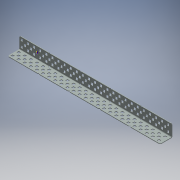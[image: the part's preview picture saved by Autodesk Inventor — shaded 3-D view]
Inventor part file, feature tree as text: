
AUTODESK INVENTOR PART (.ipt)
format: ipt  version: 2018 (Build 220112000, 112)  size: 1,527,808 bytes
history: native  units: mm (DEFAULTED — no unit token found)
features: other x154, extrude x148, sketch x12, pattern_linear x4, sheet_metal_op x3
ambient origin geometry x8: Origin, YZ Plane, XZ Plane, XY Plane, X Axis, Y Axis, Z Axis, Center Point
bodies: Solid1 (feature_tree)
feature tree (321):
  sheet_metal_op  "Face2"
  sheet_metal_op  "Flange8"
  pattern_linear  "Rectangular Pattern1"  Count1=24 Spacing1=12.7mm
  pattern_linear  "Rectangular Pattern2"  Spacing1=9.144mm  [1 undecoded]
  pattern_linear  "Rectangular Pattern3"  Spacing1=15.494mm  [1 undecoded]
  pattern_linear  "Rectangular Pattern4"  Spacing1=4.572mm  [1 undecoded]
  sketch  "Sketch23"  dims[d128=4.572mm]
  sketch  "Sketch24"  dims[d129=9.017mm d130=9.144mm d133=15.494mm d134=4.572mm d136=1.27mm d138=1.27mm d139=0.635mm d140=2.54mm d141=1.27mm d142=25.4mm d143=90.0deg d144=1.27mm d145=5.08mm d146=1.27mm d147=1.27mm d148=2.921mm d149=4.572mm d150=8.128mm d151=4.572mm d152=2.794mm d153=4.572mm d154=9.144mm d155=4.572mm d156=4.572mm d157=15.494mm d158=4.572mm d159=9.017mm d160=240.0mm d162=12.7mm d163=10.0mm d165=25.4mm d167=1.27mm d168=0.0mm d169=1.905mm d170=60.0mm d172=63.5mm d173=10.0mm d175=25.4mm d177=1.27mm d178=0.0mm d179=1.905mm d180=60.0mm d182=63.5mm d183=10.0mm d185=25.4mm d187=1.27mm d188=0.0mm d189=1.1176mm d190=1.905mm d191=40.0mm d193=63.5mm d194=10.0mm d196=25.4mm d198=1.27mm d199=0.0mm d200=25.4mm d201=0.0mm d202=250.0mm d204=12.7mm d205=20.0mm d207=12.7mm d208=25.4mm d209=0.0mm d210=240.0mm d212=12.7mm d213=0.0mm d214=0.0mm d215=0.0mm d216=0.0mm d217=0.0mm d218=0.0mm d219=0.0mm d220=0.0mm d221=0.0mm d222=0.0mm d223=0.0mm d224=0.0mm d225=0.0mm d226=0.0mm d227=0.0mm d228=0.0mm d229=0.0mm d230=0.0mm d231=0.0mm d232=0.0mm d233=0.0mm d234=0.0mm d235=0.0mm d236=0.0mm d237=0.0mm d238=0.0mm d239=0.0mm d240=0.0mm d241=0.0mm d242=0.0mm d243=0.0mm d244=0.0mm d245=0.0mm d246=0.0mm d247=0.0mm d248=0.0mm d249=0.0mm d250=0.0mm d251=0.0mm d252=0.0mm d253=0.0mm d254=0.0mm d255=0.0mm d256=0.0mm d257=0.0mm d258=0.0mm d259=0.0mm d260=0.0mm d261=0.0mm d262=0.0mm d263=0.0mm d264=0.0mm d265=0.0mm d266=0.0mm d267=0.0mm d268=0.0mm d269=0.0mm d270=0.0mm d271=0.0mm d272=0.0mm d273=0.0mm d274=0.0mm d275=0.0mm d276=0.0mm d277=0.0mm d278=0.0mm d279=0.0mm d280=0.0mm d281=0.0mm d282=0.0mm d283=0.0mm d284=0.0mm d285=0.0mm d286=0.0mm d287=0.0mm d288=0.0mm d289=0.0mm d290=0.0mm d291=0.0mm d292=0.0mm d293=0.0mm d294=0.0mm d295=0.0mm d296=0.0mm d297=0.0mm d298=0.0mm d299=0.0mm d300=0.0mm d301=0.0mm d302=0.0mm d303=0.0mm d304=0.0mm d305=0.0mm d306=0.0mm d307=0.0mm d308=0.0mm d309=0.0mm d310=0.0mm d311=0.0mm d312=0.0mm d313=0.0mm d314=0.0mm d315=0.0mm d316=0.0mm d317=0.0mm d318=0.0mm d319=0.0mm d320=0.0mm d321=0.0mm d322=0.0mm d323=0.0mm d324=0.0mm d325=0.0mm d326=0.0mm d327=0.0mm d328=0.0mm d329=0.0mm d330=0.0mm d331=0.0mm d332=0.0mm d333=0.0mm d334=0.0mm d335=0.0mm d336=0.0mm d337=0.0mm d338=0.0mm d339=0.0mm d340=0.0mm d341=0.0mm d342=0.0mm d343=0.0mm d344=0.0mm d345=0.0mm d346=0.0mm d347=0.0mm d348=0.0mm d349=0.0mm d350=0.0mm d351=0.0mm d352=0.0mm d353=0.0mm d354=0.0mm d355=0.0mm d356=0.0mm d357=0.0mm d358=0.0mm d359=0.0mm d360=25.4mm d361=0.0mm d362=250.0mm d364=12.7mm d365=20.0mm d367=12.7mm d368=25.4mm d369=0.0mm d370=240.0mm d372=12.7mm d373=0.0mm d374=0.0mm d375=0.0mm d376=0.0mm d377=0.0mm d378=0.0mm d379=0.0mm d380=0.0mm d381=0.0mm d382=0.0mm d383=0.0mm d384=0.0mm d385=0.0mm d386=0.0mm d387=0.0mm d388=0.0mm d389=0.0mm d390=0.0mm d391=0.0mm d392=0.0mm d393=0.0mm d394=0.0mm d395=0.0mm d396=0.0mm d397=0.0mm d398=0.0mm d399=0.0mm d400=0.0mm d401=0.0mm d402=0.0mm d403=0.0mm d404=0.0mm d405=0.0mm d406=0.0mm d407=0.0mm d408=0.0mm d409=0.0mm d410=0.0mm d411=0.0mm d412=0.0mm d413=0.0mm d414=0.0mm d415=0.0mm d416=0.0mm d417=0.0mm d418=0.0mm d419=0.0mm d420=0.0mm d421=0.0mm d422=0.0mm d423=0.0mm d424=0.0mm d425=0.0mm d426=0.0mm d427=0.0mm d428=0.0mm d429=0.0mm d430=0.0mm d431=0.0mm d432=0.0mm d433=0.0mm d434=0.0mm d435=0.0mm d436=0.0mm d437=0.0mm d438=0.0mm d439=0.0mm d440=0.0mm d441=0.0mm d442=0.0mm d443=0.0mm d444=0.0mm d445=0.0mm d446=0.0mm d447=0.0mm d448=0.0mm d449=0.0mm d450=0.0mm d451=0.0mm d452=0.0mm d453=0.0mm d454=0.0mm d455=0.0mm d456=0.0mm d457=0.0mm d458=0.0mm d459=0.0mm d460=0.0mm d461=0.0mm d462=0.0mm d463=0.0mm d464=0.0mm d465=0.0mm d466=0.0mm d467=0.0mm d468=0.0mm d469=0.0mm d470=0.0mm d471=0.0mm d472=0.0mm d473=0.0mm d474=0.0mm d475=0.0mm d476=0.0mm d477=0.0mm d478=0.0mm d479=0.0mm d480=0.0mm d481=0.0mm d482=0.0mm d483=0.0mm d484=0.0mm d485=0.0mm d486=0.0mm d487=0.0mm d488=0.0mm d489=0.0mm d490=0.0mm d491=0.0mm d492=0.0mm d493=0.0mm d494=0.0mm d495=0.0mm d496=0.0mm d497=0.0mm d498=0.0mm d499=0.0mm d500=0.0mm d501=0.0mm d502=0.0mm d503=0.0mm d504=0.0mm d505=0.0mm d506=0.0mm d507=0.0mm d508=0.0mm d509=0.0mm d510=0.0mm d511=0.0mm d512=0.0mm d513=0.0mm d514=0.0mm d515=0.0mm d516=0.0mm d517=0.0mm d518=0.0mm d519=0.0mm d520=0.0mm d521=1.27mm]
  sketch  "Sketch1"  dims[d20=2.794mm]
  other  "Plate9"
  sketch  "Sketch14"  dims[d22=2.921mm]
  other  "Plate10"
  sheet_metal_op  "Bend8"
  sketch  "Sketch15"  dims[d23=22.86mm]
  sketch  "Sketch16"  dims[d24=4.572mm]
  sketch  "Sketch17"  dims[d25=8.128mm]
  sketch  "Sketch18"  dims[d26=4.572mm]
  sketch  "Sketch19"  dims[d27=1.27mm]
  other  "Srf1"
  other  "Srf2"
  other  "Srf3"
  other  "Srf4"
  other  "Srf5"
  other  "Srf6"
  other  "Srf7"
  other  "Srf8"
  other  "Srf9"
  other  "Srf10"
  other  "Srf11"
  other  "Srf12"
  other  "Srf13"
  other  "Srf14"
  other  "Srf15"
  other  "Srf16"
  other  "Srf17"
  other  "Srf18"
  other  "Srf19"
  other  "Srf20"
  other  "Srf21"
  other  "Srf22"
  other  "Srf23"
  other  "Srf24"
  other  "Srf25"
  other  "Srf26"
  other  "Srf27"
  other  "Srf28"
  other  "Srf29"
  other  "Srf30"
  other  "Srf31"
  other  "Srf32"
  other  "Srf33"
  other  "Srf34"
  other  "Srf35"
  other  "Srf36"
  other  "Srf37"
  other  "Srf38"
  other  "Srf39"
  other  "Srf40"
  other  "Srf41"
  other  "Srf42"
  other  "Srf43"
  other  "Srf44"
  other  "Srf45"
  other  "Srf46"
  other  "Srf47"
  other  "Srf48"
  other  "Srf49"
  other  "Srf50"
  sketch  "Sketch20"  dims[d125=317.5mm]
  other  "Srf51"
  other  "Srf52"
  other  "Srf53"
  other  "Srf54"
  other  "Srf55"
  other  "Srf56"
  other  "Srf57"
  other  "Srf58"
  other  "Srf59"
  other  "Srf60"
  other  "Srf61"
  other  "Srf62"
  other  "Srf63"
  other  "Srf64"
  other  "Srf65"
  other  "Srf66"
  other  "Srf67"
  other  "Srf68"
  other  "Srf69"
  other  "Srf70"
  other  "Srf71"
  other  "Srf72"
  other  "Srf73"
  other  "Srf74"
  sketch  "Sketch21"  dims[d126=4.572mm]
  other  "Srf75"
  other  "Srf76"
  other  "Srf77"
  other  "Srf78"
  other  "Srf79"
  other  "Srf80"
  other  "Srf81"
  other  "Srf82"
  other  "Srf83"
  other  "Srf84"
  other  "Srf85"
  other  "Srf86"
  other  "Srf87"
  other  "Srf88"
  other  "Srf89"
  other  "Srf90"
  other  "Srf91"
  other  "Srf92"
  other  "Srf93"
  other  "Srf94"
  other  "Srf95"
  other  "Srf96"
  other  "Srf97"
  other  "Srf98"
  other  "Srf99"
  other  "Srf100"
  other  "Srf101"
  other  "Srf102"
  other  "Srf103"
  other  "Srf104"
  other  "Srf105"
  other  "Srf106"
  other  "Srf107"
  other  "Srf108"
  other  "Srf109"
  other  "Srf110"
  other  "Srf111"
  other  "Srf112"
  other  "Srf113"
  other  "Srf114"
  other  "Srf115"
  other  "Srf116"
  other  "Srf117"
  other  "Srf118"
  other  "Srf119"
  other  "Srf120"
  other  "Srf121"
  other  "Srf122"
  other  "Srf123"
  other  "Srf124"
  sketch  "Sketch22"  dims[d127=4.572mm]
  other  "Srf125"
  other  "Srf126"
  other  "Srf127"
  other  "Srf128"
  other  "Srf129"
  other  "Srf130"
  other  "Srf131"
  other  "Srf132"
  other  "Srf133"
  other  "Srf134"
  other  "Srf135"
  other  "Srf136"
  other  "Srf137"
  other  "Srf138"
  other  "Srf139"
  other  "Srf140"
  other  "Srf141"
  other  "Srf142"
  other  "Srf143"
  other  "Srf144"
  other  "Srf145"
  other  "Srf146"
  other  "Srf147"
  other  "Srf148"
  other  "Cut4"
  other  "Cut5"
  other  "Cut6"
  other  "Cut7"
  extrude  "ExtrusionSrf1"  Depth=10.0mm
  extrude  "ExtrusionSrf51"  Depth=10.0mm
  extrude  "ExtrusionSrf75"  Depth=10.0mm
  extrude  "ExtrusionSrf125"  Depth=10.0mm
  extrude  "ExtrusionSrf2"  Depth=10.0mm
  extrude  "ExtrusionSrf3"  Depth=10.0mm TaperAngle=90.0deg
  extrude  "ExtrusionSrf4"  Depth=10.0mm
  extrude  "ExtrusionSrf5"  Depth=10.0mm
  extrude  "ExtrusionSrf6"  Depth=10.0mm
  extrude  "ExtrusionSrf7"  Depth=10.0mm
  extrude  "ExtrusionSrf8"  Depth=10.0mm
  extrude  "ExtrusionSrf9"  Depth=10.0mm
  extrude  "ExtrusionSrf10"  Depth=10.0mm
  extrude  "ExtrusionSrf11"  Depth=10.0mm
  extrude  "ExtrusionSrf12"  Depth=10.0mm
  extrude  "ExtrusionSrf13"  Depth=10.0mm
  extrude  "ExtrusionSrf14"  Depth=10.0mm
  extrude  "ExtrusionSrf15"  Depth=10.0mm
  extrude  "ExtrusionSrf16"  Depth=10.0mm
  extrude  "ExtrusionSrf17"  Depth=10.0mm
  extrude  "ExtrusionSrf18"  Depth=10.0mm
  extrude  "ExtrusionSrf19"  Depth=10.0mm
  extrude  "ExtrusionSrf20"  Depth=10.0mm
  extrude  "ExtrusionSrf21"  TaperAngle=0.0deg  [1 undecoded]
  extrude  "ExtrusionSrf22"  Depth=10.0mm
  extrude  "ExtrusionSrf23"  Depth=10.0mm
  extrude  "ExtrusionSrf24"  Depth=10.0mm
  extrude  "ExtrusionSrf25"  TaperAngle=0.0deg  [1 undecoded]
  extrude  "ExtrusionSrf26"  Depth=10.0mm
  extrude  "ExtrusionSrf27"  Depth=10.0mm
  extrude  "ExtrusionSrf28"  Depth=10.0mm
  extrude  "ExtrusionSrf29"  TaperAngle=0.0deg  [1 undecoded]
  extrude  "ExtrusionSrf30"  Depth=10.0mm
  extrude  "ExtrusionSrf31"  Depth=10.0mm
  extrude  "ExtrusionSrf32"  Depth=10.0mm
  extrude  "ExtrusionSrf33"  Depth=10.0mm
  extrude  "ExtrusionSrf34"  TaperAngle=0.0deg  [1 undecoded]
  extrude  "ExtrusionSrf35"  Depth=10.0mm TaperAngle=0.0deg
  extrude  "ExtrusionSrf36"  Depth=10.0mm
  extrude  "ExtrusionSrf37"  Depth=10.0mm
  extrude  "ExtrusionSrf38"  Depth=10.0mm TaperAngle=0.0deg
  extrude  "ExtrusionSrf39"  Depth=10.0mm
  extrude  "ExtrusionSrf40"  TaperAngle=0.0deg  [1 undecoded]
  extrude  "ExtrusionSrf41"  TaperAngle=0.0deg  [1 undecoded]
  extrude  "ExtrusionSrf42"  TaperAngle=0.0deg  [1 undecoded]
  extrude  "ExtrusionSrf43"  TaperAngle=0.0deg  [1 undecoded]
  extrude  "ExtrusionSrf44"  TaperAngle=0.0deg  [1 undecoded]
  extrude  "ExtrusionSrf45"  TaperAngle=0.0deg  [1 undecoded]
  extrude  "ExtrusionSrf46"  TaperAngle=0.0deg  [1 undecoded]
  extrude  "ExtrusionSrf47"  TaperAngle=0.0deg  [1 undecoded]
  extrude  "ExtrusionSrf48"  TaperAngle=0.0deg  [1 undecoded]
  extrude  "ExtrusionSrf49"  TaperAngle=0.0deg  [1 undecoded]
  extrude  "ExtrusionSrf50"  TaperAngle=0.0deg  [1 undecoded]
  extrude  "ExtrusionSrf52"  TaperAngle=0.0deg  [1 undecoded]
  extrude  "ExtrusionSrf53"  TaperAngle=0.0deg  [1 undecoded]
  extrude  "ExtrusionSrf54"  TaperAngle=0.0deg  [1 undecoded]
  extrude  "ExtrusionSrf55"  TaperAngle=0.0deg  [1 undecoded]
  extrude  "ExtrusionSrf56"  TaperAngle=0.0deg  [1 undecoded]
  extrude  "ExtrusionSrf57"  TaperAngle=0.0deg  [1 undecoded]
  extrude  "ExtrusionSrf58"  TaperAngle=0.0deg  [1 undecoded]
  extrude  "ExtrusionSrf59"  TaperAngle=0.0deg  [1 undecoded]
  extrude  "ExtrusionSrf60"  TaperAngle=0.0deg  [1 undecoded]
  extrude  "ExtrusionSrf61"  TaperAngle=0.0deg  [1 undecoded]
  extrude  "ExtrusionSrf62"  TaperAngle=0.0deg  [1 undecoded]
  extrude  "ExtrusionSrf63"  TaperAngle=0.0deg  [1 undecoded]
  extrude  "ExtrusionSrf64"  TaperAngle=0.0deg  [1 undecoded]
  extrude  "ExtrusionSrf65"  TaperAngle=0.0deg  [1 undecoded]
  extrude  "ExtrusionSrf66"  TaperAngle=0.0deg  [1 undecoded]
  extrude  "ExtrusionSrf67"  TaperAngle=0.0deg  [1 undecoded]
  extrude  "ExtrusionSrf68"  TaperAngle=0.0deg  [1 undecoded]
  extrude  "ExtrusionSrf69"  TaperAngle=0.0deg  [1 undecoded]
  extrude  "ExtrusionSrf70"  TaperAngle=0.0deg  [1 undecoded]
  extrude  "ExtrusionSrf71"  TaperAngle=0.0deg  [1 undecoded]
  extrude  "ExtrusionSrf72"  TaperAngle=0.0deg  [1 undecoded]
  extrude  "ExtrusionSrf73"  TaperAngle=0.0deg  [1 undecoded]
  extrude  "ExtrusionSrf74"  TaperAngle=0.0deg  [1 undecoded]
  extrude  "ExtrusionSrf76"  TaperAngle=0.0deg  [1 undecoded]
  extrude  "ExtrusionSrf77"  TaperAngle=0.0deg  [1 undecoded]
  extrude  "ExtrusionSrf78"  TaperAngle=0.0deg  [1 undecoded]
  extrude  "ExtrusionSrf79"  TaperAngle=0.0deg  [1 undecoded]
  extrude  "ExtrusionSrf80"  TaperAngle=0.0deg  [1 undecoded]
  extrude  "ExtrusionSrf81"  TaperAngle=0.0deg  [1 undecoded]
  extrude  "ExtrusionSrf82"  TaperAngle=0.0deg  [1 undecoded]
  extrude  "ExtrusionSrf83"  TaperAngle=0.0deg  [1 undecoded]
  extrude  "ExtrusionSrf84"  TaperAngle=0.0deg  [1 undecoded]
  extrude  "ExtrusionSrf85"  TaperAngle=0.0deg  [1 undecoded]
  extrude  "ExtrusionSrf86"  TaperAngle=0.0deg  [1 undecoded]
  extrude  "ExtrusionSrf87"  TaperAngle=0.0deg  [1 undecoded]
  extrude  "ExtrusionSrf88"  TaperAngle=0.0deg  [1 undecoded]
  extrude  "ExtrusionSrf89"  TaperAngle=0.0deg  [1 undecoded]
  extrude  "ExtrusionSrf90"  TaperAngle=0.0deg  [1 undecoded]
  extrude  "ExtrusionSrf91"  TaperAngle=0.0deg  [1 undecoded]
  extrude  "ExtrusionSrf92"  TaperAngle=0.0deg  [1 undecoded]
  extrude  "ExtrusionSrf93"  TaperAngle=0.0deg  [1 undecoded]
  extrude  "ExtrusionSrf94"  TaperAngle=0.0deg  [1 undecoded]
  extrude  "ExtrusionSrf95"  TaperAngle=0.0deg  [1 undecoded]
  extrude  "ExtrusionSrf96"  TaperAngle=0.0deg  [1 undecoded]
  extrude  "ExtrusionSrf97"  TaperAngle=0.0deg  [1 undecoded]
  extrude  "ExtrusionSrf98"  TaperAngle=0.0deg  [1 undecoded]
  extrude  "ExtrusionSrf99"  TaperAngle=0.0deg  [1 undecoded]
  extrude  "ExtrusionSrf100"  TaperAngle=0.0deg  [1 undecoded]
  extrude  "ExtrusionSrf101"  TaperAngle=0.0deg  [1 undecoded]
  extrude  "ExtrusionSrf102"  TaperAngle=0.0deg  [1 undecoded]
  extrude  "ExtrusionSrf103"  TaperAngle=0.0deg  [1 undecoded]
  extrude  "ExtrusionSrf104"  TaperAngle=0.0deg  [1 undecoded]
  extrude  "ExtrusionSrf105"  TaperAngle=0.0deg  [1 undecoded]
  extrude  "ExtrusionSrf106"  TaperAngle=0.0deg  [1 undecoded]
  extrude  "ExtrusionSrf107"  TaperAngle=0.0deg  [1 undecoded]
  extrude  "ExtrusionSrf108"  TaperAngle=0.0deg  [1 undecoded]
  extrude  "ExtrusionSrf109"  TaperAngle=0.0deg  [1 undecoded]
  extrude  "ExtrusionSrf110"  TaperAngle=0.0deg  [1 undecoded]
  extrude  "ExtrusionSrf111"  TaperAngle=0.0deg  [1 undecoded]
  extrude  "ExtrusionSrf112"  TaperAngle=0.0deg  [1 undecoded]
  extrude  "ExtrusionSrf113"  TaperAngle=0.0deg  [1 undecoded]
  extrude  "ExtrusionSrf114"  TaperAngle=0.0deg  [1 undecoded]
  extrude  "ExtrusionSrf115"  TaperAngle=0.0deg  [1 undecoded]
  extrude  "ExtrusionSrf116"  TaperAngle=0.0deg  [1 undecoded]
  extrude  "ExtrusionSrf117"  TaperAngle=0.0deg  [1 undecoded]
  extrude  "ExtrusionSrf118"  TaperAngle=0.0deg  [1 undecoded]
  extrude  "ExtrusionSrf119"  TaperAngle=0.0deg  [1 undecoded]
  extrude  "ExtrusionSrf120"  TaperAngle=0.0deg  [1 undecoded]
  extrude  "ExtrusionSrf121"  TaperAngle=0.0deg  [1 undecoded]
  extrude  "ExtrusionSrf122"  TaperAngle=0.0deg  [1 undecoded]
  extrude  "ExtrusionSrf123"  TaperAngle=0.0deg  [1 undecoded]
  extrude  "ExtrusionSrf124"  TaperAngle=0.0deg  [1 undecoded]
  extrude  "ExtrusionSrf126"  TaperAngle=0.0deg  [1 undecoded]
  extrude  "ExtrusionSrf127"  TaperAngle=0.0deg  [1 undecoded]
  extrude  "ExtrusionSrf128"  TaperAngle=0.0deg  [1 undecoded]
  extrude  "ExtrusionSrf129"  TaperAngle=0.0deg  [1 undecoded]
  extrude  "ExtrusionSrf130"  TaperAngle=0.0deg  [1 undecoded]
  extrude  "ExtrusionSrf131"  TaperAngle=0.0deg  [1 undecoded]
  extrude  "ExtrusionSrf132"  TaperAngle=0.0deg  [1 undecoded]
  extrude  "ExtrusionSrf133"  TaperAngle=0.0deg  [1 undecoded]
  extrude  "ExtrusionSrf134"  TaperAngle=0.0deg  [1 undecoded]
  extrude  "ExtrusionSrf135"  TaperAngle=0.0deg  [1 undecoded]
  extrude  "ExtrusionSrf136"  TaperAngle=0.0deg  [1 undecoded]
  extrude  "ExtrusionSrf137"  TaperAngle=0.0deg  [1 undecoded]
  extrude  "ExtrusionSrf138"  TaperAngle=0.0deg  [1 undecoded]
  extrude  "ExtrusionSrf139"  TaperAngle=0.0deg  [1 undecoded]
  extrude  "ExtrusionSrf140"  TaperAngle=0.0deg  [1 undecoded]
  extrude  "ExtrusionSrf141"  TaperAngle=0.0deg  [1 undecoded]
  extrude  "ExtrusionSrf142"  TaperAngle=0.0deg  [1 undecoded]
  extrude  "ExtrusionSrf143"  TaperAngle=0.0deg  [1 undecoded]
  extrude  "ExtrusionSrf144"  TaperAngle=0.0deg  [1 undecoded]
  extrude  "ExtrusionSrf145"  TaperAngle=0.0deg  [1 undecoded]
  extrude  "ExtrusionSrf146"  TaperAngle=0.0deg  [1 undecoded]
  extrude  "ExtrusionSrf147"  TaperAngle=0.0deg  [1 undecoded]
  extrude  "ExtrusionSrf148"  TaperAngle=0.0deg  [1 undecoded]
note: 113 required parameter values undecoded (feature->parameter linkage not recoverable at this tier; creation-order binding heuristic only, values carry confidence <= 0.55)
